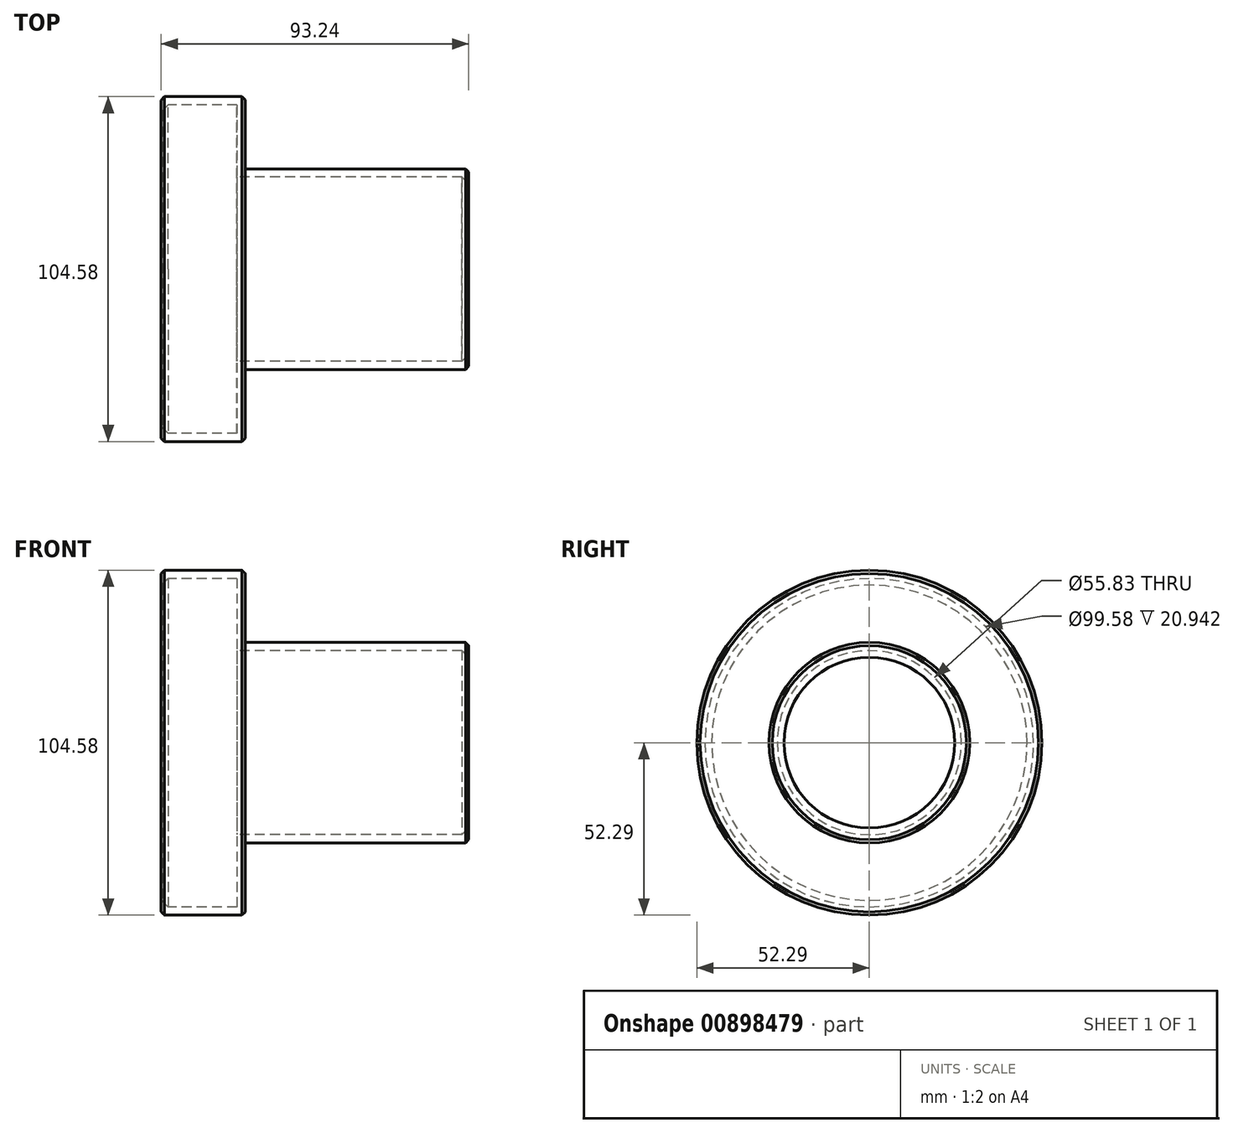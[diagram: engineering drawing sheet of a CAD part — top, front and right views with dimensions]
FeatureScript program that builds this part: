
annotation { "Feature Type Name" : "Feature", "Feature Type Description" : "" }
export const myFeature = defineFeature(function(context is Context, id is Id, definition is map)
    precondition{}
    {
        {
            var Q0;
            Q0=qCreatedBy(makeId("Top.planeOp"),FACE);
            var sketch = newSketch(context, id + "F0", { "sketchPlane" : qUnion([Q0])});
            skLineSegment(sketch, "E0", {"start": v(28.3, 0) * mm, "end": v(28.3, 30.42) * mm});
            skLineSegment(sketch, "E1", {"start": v(28.3, 30.42) * mm, "end": v(-39.43, 30.42) * mm});
            skLineSegment(sketch, "E2", {"start": v(-39.43, 30.42) * mm, "end": v(-39.43, 52.3) * mm});
            skLineSegment(sketch, "E3", {"start": v(-39.43, 52.3) * mm, "end": v(-65.01, 52.3) * mm});
            skLineSegment(sketch, "E4", {"start": v(-65.01, 52.3) * mm, "end": v(-61.85, 0) * mm});
            skLineSegment(sketch, "E5", {"start": v(-61.85, 0) * mm, "end": v(28.3, 0) * mm});
            skSolve(sketch);
        }
        {
            var Q0;
            Q0 = qSketchRegion(id + "F0", true);
            var Q1;
            Q1=sQuery(id+"F0.wireOp",EDGE,"E5");
            revolve(context, id + "F1", {"surfaceOperationType" : NewSurfaceOperationType.NEW, "entities" : qUnion([Q0]), "axis" : qUnion([Q1]), "revolveType" : RevolveType.FULL});
        }
        {
            var Q0;
            Q0=makeQuery(id+"F1.opRevolve","SWEPT_EDGE",EDGE,{"disambiguationData":[OSD([sQuery(id+"F0.wireOp",EDGE,"E0"),sQuery(id+"F0.wireOp",EDGE,"E1")])]});
            var Q1;
            Q1=makeQuery(id+"F1.opRevolve","SWEPT_EDGE",EDGE,{"disambiguationData":[OSD([sQuery(id+"F0.wireOp",EDGE,"E2"),sQuery(id+"F0.wireOp",EDGE,"E3")])]});
            var Q2;
            Q2=makeQuery(id+"F1.opRevolve","SWEPT_EDGE",EDGE,{"disambiguationData":[OSD([sQuery(id+"F0.wireOp",EDGE,"E3"),sQuery(id+"F0.wireOp",EDGE,"E4")])]});
            chamfer(context, id + "F2", {"entities" : qUnion([Q0, Q1, Q2]), "width" : 1 * mm, "tangentPropagation" : true});
        }
        {
            var Q0;
            Q0=makeQuery(id+"F1.opRevolve","SWEPT_FACE",FACE,{"disambiguationData":[OSD([sQuery(id+"F0.wireOp",EDGE,"E4")])]});
            var Q1;
            Q1=makeQuery(id+"F1.opRevolve","SWEPT_FACE",FACE,{"disambiguationData":[OSD([sQuery(id+"F0.wireOp",EDGE,"E0")])]});
            shell(context, id + "F3", {"entities" : qUnion([Q0, Q1]), "thickness" : 2.5 * mm});
        }
    });
